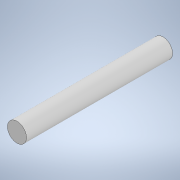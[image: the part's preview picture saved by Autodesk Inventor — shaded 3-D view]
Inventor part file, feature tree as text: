
AUTODESK INVENTOR PART (.ipt)
format: ipt  version: 2020 (Build 240168000, 168)  size: 90,112 bytes
history: native  units: mm
features: extrude x1, sketch x1
ambient origin geometry x8: Origin, YZ Plane, XZ Plane, XY Plane, X Axis, Y Axis, Z Axis, Center Point
bodies: Solid1 (feature_tree)
feature tree (2):
  extrude  "Extrusion1"  Depth=23.0mm TaperAngle=0.0deg
  sketch  "Sketch1"  dims[d0=3.0mm d1=23.0mm d2=0.0mm]
